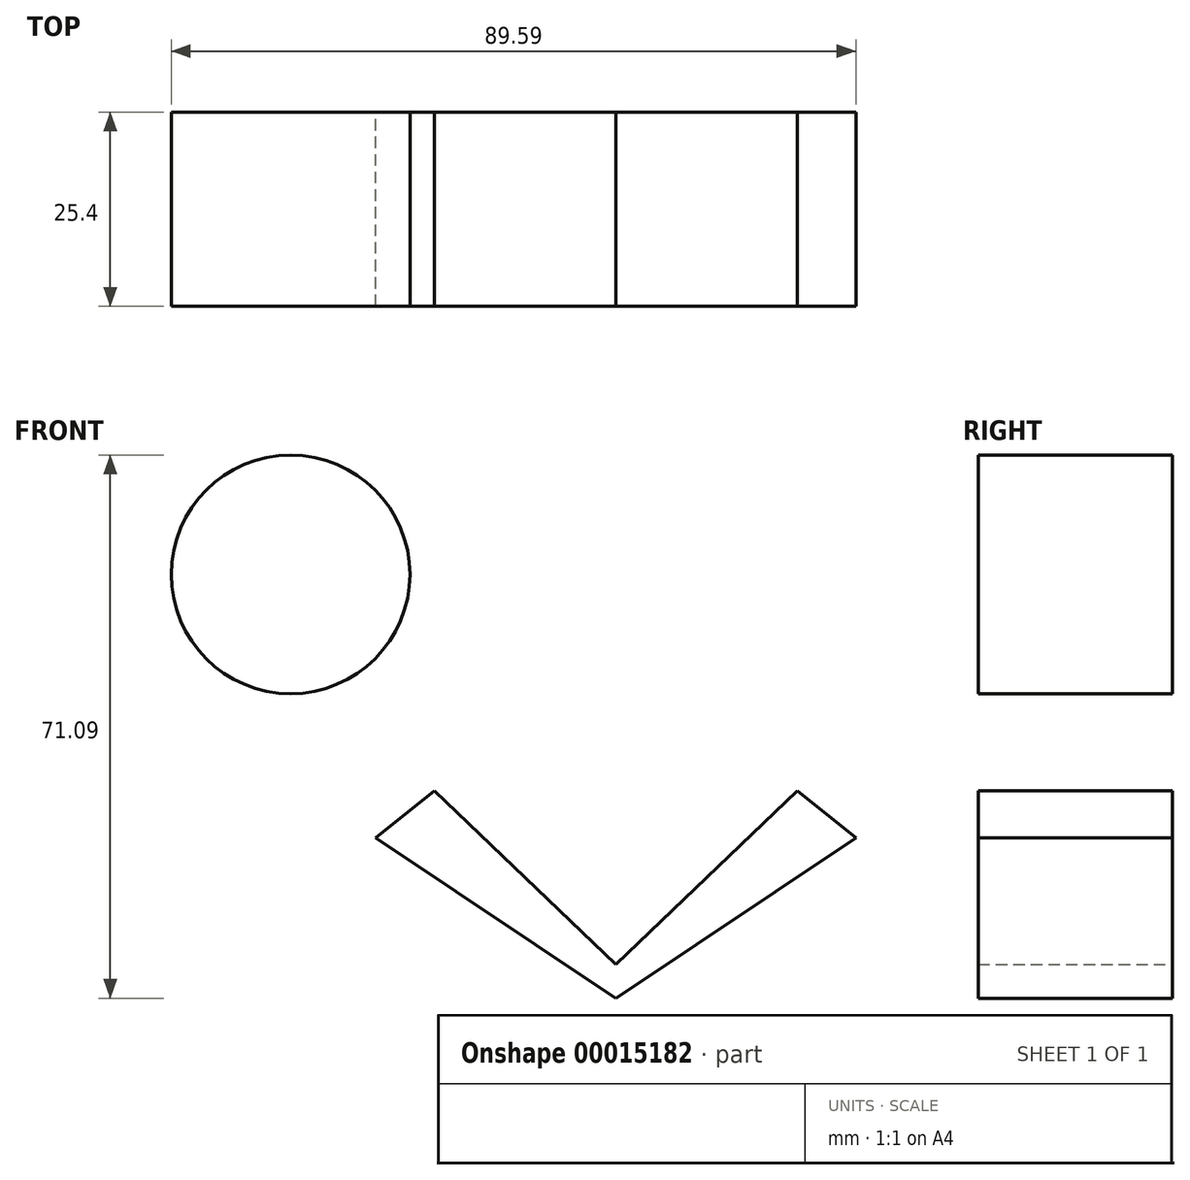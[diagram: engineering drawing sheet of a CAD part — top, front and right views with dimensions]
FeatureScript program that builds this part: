
annotation { "Feature Type Name" : "Feature", "Feature Type Description" : "" }
export const myFeature = defineFeature(function(context is Context, id is Id, definition is map)
    precondition{}
    {
        {
            var Q0;
            Q0=qCreatedBy(makeId("Front.planeOp"),FACE);
            var sketch = newSketch(context, id + "F0", { "sketchPlane" : qUnion([Q0])});
            skCircle(sketch, "E0", {"center": v(-42.57, 0) * mm, "radius": 15.61 * mm});
            skCircle(sketch, "E1.MirrorC", {"center": v(42.57, 0) * mm, "radius": 15.61 * mm});
            skSolve(sketch);
        }
        {
            var Q0;
            Q0=qCreatedBy(makeId("Front.planeOp"),FACE);
            var sketch = newSketch(context, id + "F1", { "sketchPlane" : qUnion([Q0])});
            skLineSegment(sketch, "E2", {"start": v(0, -55.48) * mm, "end": v(-31.4, -34.46) * mm});
            skLineSegment(sketch, "E3", {"start": v(-31.4, -34.46) * mm, "end": v(-23.75, -28.36) * mm});
            skLineSegment(sketch, "E4", {"start": v(-23.75, -28.36) * mm, "end": v(0, -51.07) * mm});
            skLineSegment(sketch, "E5", {"start": v(0, -51.07) * mm, "end": v(0, -55.48) * mm});
            skLineSegment(sketch, "E6.MirrorCS", {"start": v(23.75, -28.36) * mm, "end": v(0, -51.07) * mm});
            skLineSegment(sketch, "E7.MirrorCS", {"start": v(31.4, -34.46) * mm, "end": v(23.75, -28.36) * mm});
            skLineSegment(sketch, "E8.MirrorCS", {"start": v(0, -55.48) * mm, "end": v(31.4, -34.46) * mm});
            skSolve(sketch);
        }
        {
            var Q0;
            Q0=makeQuery(id+"F0.imprint","IMPRINT",FACE,{"disambiguationData":[TD([[makeQuery(id+"F0.imprint","IMPRINT",EDGE,{"derivedFrom":sQuery(id+"F0.wireOp",EDGE,"E0")}),1.0]])]});
            var Q1;
            Q1=makeQuery(id+"F0.imprint","IMPRINT",FACE,{"disambiguationData":[TD([[makeQuery(id+"F0.imprint","IMPRINT",EDGE,{"derivedFrom":sQuery(id+"F0.wireOp",EDGE,"E1.MirrorC")}),-1.0]])]});
            extrude(context, id + "F2", {"entities" : qUnion([Q0, Q1]), "depth" : 25.4 * mm});
        }
        {
            var Q0;
            Q0=makeQuery(id+"F1.imprint","IMPRINT",FACE,{"disambiguationData":[TD([[makeQuery(id+"F1.imprint","IMPRINT",EDGE,{"derivedFrom":sQuery(id+"F1.wireOp",EDGE,"E2")}),-1.0]])]});
            var Q1;
            Q1=makeQuery(id+"F1.imprint","IMPRINT",FACE,{"disambiguationData":[TD([[makeQuery(id+"F1.imprint","IMPRINT",EDGE,{"derivedFrom":sQuery(id+"F1.wireOp",EDGE,"E5")}),1.0]])]});
            extrude(context, id + "F3", {"entities" : qUnion([Q0, Q1]), "depth" : 25.4 * mm});
        }
    });
